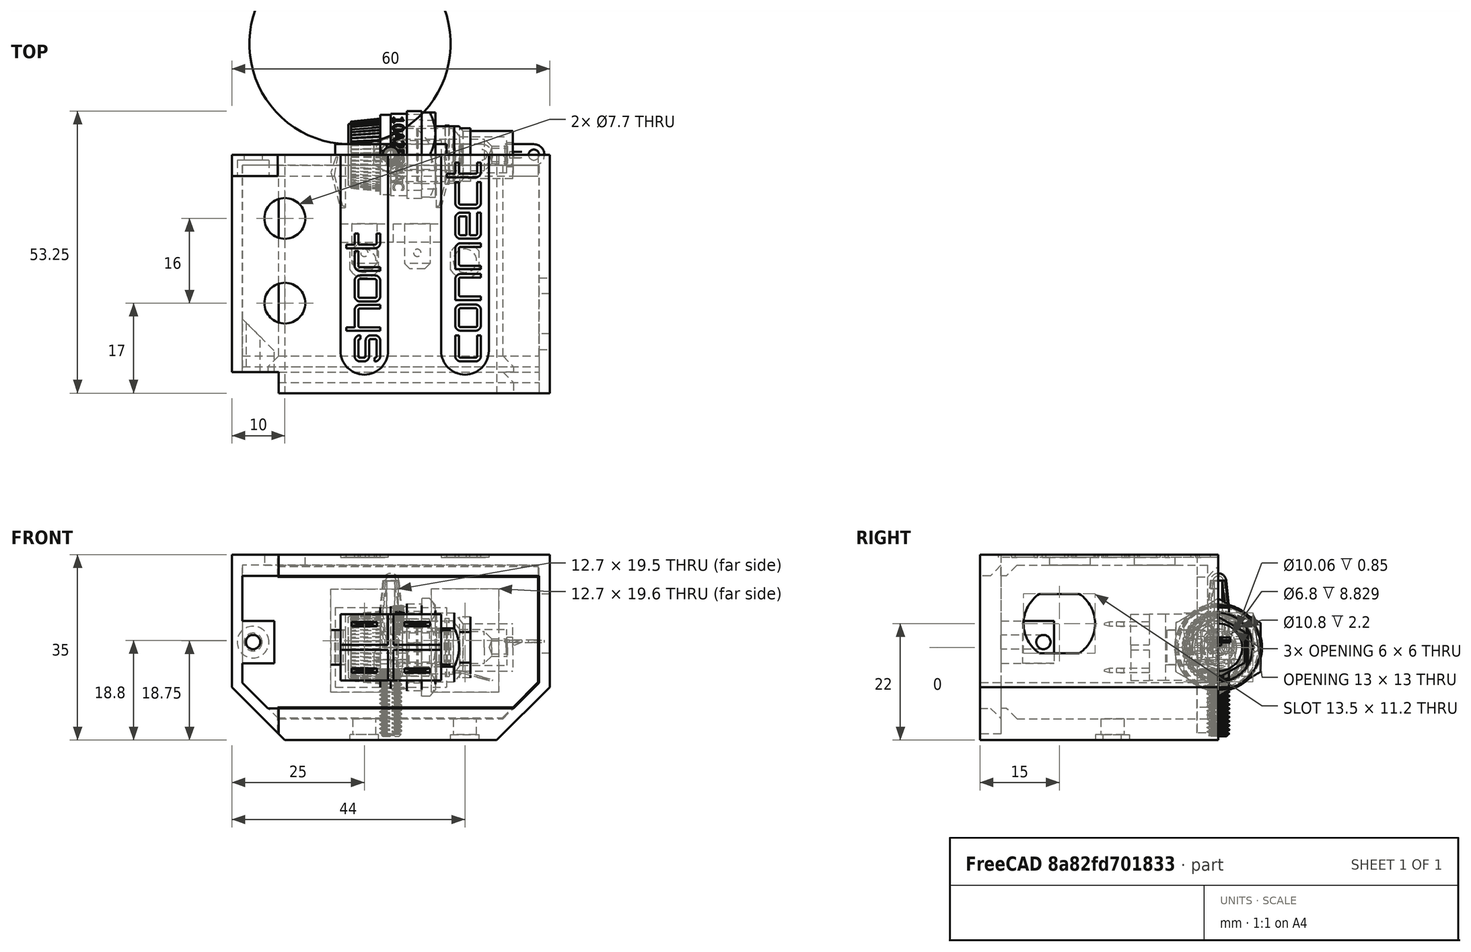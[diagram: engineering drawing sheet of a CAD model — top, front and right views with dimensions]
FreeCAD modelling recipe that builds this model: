
FCSTD DOCUMENT  (FreeCAD 1.0R38641 +468 (Git))
Label: multimeter_module
License: All rights reserved
LicenseURL: http://en.wikipedia.org/wiki/All_rights_reserved
objects: Sketcher::SketchObject×18, PartDesign::Pocket×12, Part::FeaturePython×11, App::Link×9, App::FeaturePython×9, Part::Part2DObjectPython×8, PartDesign::Body×6, PartDesign::Pad×5, Part::Feature×4, PartDesign::FeatureBase×4, PartDesign::Plane×3, PartDesign::Mirrored×3, App::DocumentObjectGroup×2, Part::Extrusion×2, Spreadsheet::Sheet×1, Image::ImagePlane×1, PartDesign::ShapeBinder×1, PartDesign::Line×1, PartDesign::Groove×1, Part::MultiFuse×1, +2 more types
note: 141 computed .brp shape members not serialized (recipe doc carries the construction recipe); baked Part::Feature solids carry a one-line shape summary decoded from their .brp

FEATURE [Spreadsheet::Sheet] Spreadsheet
  cells = B1='Print; C1='Nominal; A2='Length; B2(Length)=60; A3='Width; B3(Width)=45; A4='Height; B4(Height)=35; A5='Thickness; B5(Thickness)=2; A6='ThicknessBottom; B6(ThicknessBottom)=4; A7='SwitchWidth; B7(SwitchWidth)=12.7; C7=12.5; A8='SwitchHeight; B8(SwitchHeight)=19.6; C8=19; A9='SwitchDistance; B9(SwitchDistance)=19; A10='PlugDiameter; B10(PlugDiameter)=4.4; C10=4; A11='PlugPocketLength; B11(PlugPocketLength)=6.4; C11=6; A12='PlugPocketWidth; B12(PlugPocketWidth)=5.4; C12=5; A13='PlugDistance; B13(PlugDistance)=19; A14='PlugOffset; B14(PlugOffset)=16; A15='SocketDiameter; B15(SocketDiameter)=7.7; C15=7.3; A16='SocketDistance; B16(SocketDistance)=16; A17='FuseWidth; B17(FuseWidth)=11.2; C17=11.2; A18='FuseHeight; B18(FuseHeight)=13.5; C18=13.5; A19='PullChamferDepth; B19(PullChamferDepth)=10; A20='ThreadedHoleDiameter; B20(ThreadedHoleDiameter)=2.7; C20=3; A21='ScrewHoleRadius; B21(ScrewHoleRadius)=1.7; C21=1.5; A22='ScrewHeadRadius; B22(ScrewHeadRadius)=3
FEATURE [Sketcher::SketchObject] Sketch
  ArcFitTolerance = 1e-06
  AttachmentSupport = -> [XZ_Plane]
  FullyConstrained = true
  MakeInternals = false
  MapMode = 5
  Placement = pos=(0,0,0) rot=(1,0,0;1.5708rad)
  expr: Constraints[10] = Spreadsheet.Height
  expr: Constraints[9] = Spreadsheet.Length
  sketch-geometry (5):
    g0: LineSegment StartX=-30 StartY=-17.5 StartZ=0 EndX=30 EndY=-17.5 EndZ=0
    g1: LineSegment StartX=30 StartY=-17.5 StartZ=0 EndX=30 EndY=17.5 EndZ=0
    g2: LineSegment StartX=30 StartY=17.5 StartZ=0 EndX=-30 EndY=17.5 EndZ=0
    g3: LineSegment StartX=-30 StartY=17.5 StartZ=0 EndX=-30 EndY=-17.5 EndZ=0
    g4: GeomPoint [constr] X=0 Y=0 Z=0
  constraints (12):
    c: Coincident(g0,g1)
    c: Coincident(g1,g2)
    c: Coincident(g2,g3)
    c: Coincident(g3,g0)
    c: Horizontal(g0)
    c: Horizontal(g2)
    c: Vertical(g1)
    c: Vertical(g3)
    c: Symmetric(g2,g0,g4)
    c: Distance(g1,g3) = 60
    c: Distance(g0,g2) = 35
    c: Coincident(g4,g-1)
FEATURE [PartDesign::Pad] Pad
  Direction = (0,-1,2e-16)
  Length = 45
  Length2 = 10
  Placement = pos=(0,0,0) rot=(1,0,0;1.5708rad)
  Profile = -> Sketch
  ReferenceAxis = -> Sketch [N_Axis]
  Refine = true
  Suppressed = false
  Type = 0
  expr: Length = Spreadsheet.Width
FEATURE [Sketcher::SketchObject] Sketch001
  ArcFitTolerance = 1e-06
  AttachmentSupport = -> [Pad]
  ExternalGeometry = -> [Pad]
  FullyConstrained = true
  MakeInternals = false
  MapMode = 5
  Placement = pos=(0,-45,0) rot=(1,0,0;1.5708rad)
  expr: Constraints[10] = Spreadsheet.Length - 2 * Spreadsheet.Thickness
  expr: Constraints[11] = Spreadsheet.Thickness
  expr: Constraints[12] = Spreadsheet.Thickness
  expr: Constraints[9] = Spreadsheet.Height - Spreadsheet.Thickness - Spreadsheet.ThicknessBottom
  sketch-geometry (5):
    g0: LineSegment StartX=28 StartY=-13.5 StartZ=0 EndX=28 EndY=15.5 EndZ=0
    g1: LineSegment StartX=28 StartY=15.5 StartZ=0 EndX=-28 EndY=15.5 EndZ=0
    g2: LineSegment StartX=-28 StartY=15.5 StartZ=0 EndX=-28 EndY=-13.5 EndZ=0
    g3: LineSegment StartX=-28 StartY=-13.5 StartZ=0 EndX=28 EndY=-13.5 EndZ=0
    g4: GeomPoint [constr] X=0 Y=0 Z=0
  constraints (13):
    c: Coincident(g0,g1)
    c: Coincident(g1,g2)
    c: Coincident(g2,g3)
    c: Coincident(g3,g0)
    c: Vertical(g0)
    c: Vertical(g2)
    c: Horizontal(g1)
    c: Horizontal(g3)
    c: Coincident(g4,g-1)
    c: DistanceY(g0,g0) = 29
    c: DistanceX(g3,g3) = 56
    c: Distance(g-4,g1) = 2
    c: Distance(g-3,g2) = 2
FEATURE [PartDesign::Pocket] Pocket  label="Box inside"
  BaseFeature = -> Pad
  Direction = (0,1,-2e-16)
  Length = 43
  Length2 = 5
  Placement = pos=(0,0,0) rot=(1,0,0;1.5708rad)
  Profile = -> Sketch001
  ReferenceAxis = -> Sketch001 [N_Axis]
  Refine = true
  Suppressed = false
  Type = 0
  expr: Length = Spreadsheet.Width - Spreadsheet.Thickness
FEATURE [Sketcher::SketchObject] Sketch003
  ArcFitTolerance = 1e-06
  AttachmentSupport = -> [Pocket]
  ExternalGeometry = -> [Pocket]
  FullyConstrained = true
  MakeInternals = false
  MapMode = 5
  Placement = pos=(0,0,0) rot=(-1,0,0;1.5708rad)
  expr: Constraints[19] = Spreadsheet.SwitchWidth
  expr: Constraints[21] = Spreadsheet.SwitchDistance
  expr: Constraints[26] = Spreadsheet.PlugOffset
  expr: Constraints[8] = Spreadsheet.SwitchWidth
  expr: Constraints[9] = Spreadsheet.SwitchHeight
  sketch-geometry (11):
    g0: LineSegment StartX=7.65 StartY=-11.1 StartZ=0 EndX=20.35 EndY=-11.1 EndZ=0
    g1: LineSegment StartX=20.35 StartY=-11.1 StartZ=0 EndX=20.35 EndY=8.5 EndZ=0
    g2: LineSegment StartX=20.35 StartY=8.5 StartZ=0 EndX=7.65 EndY=8.5 EndZ=0
    g3: LineSegment StartX=7.65 StartY=8.5 StartZ=0 EndX=7.65 EndY=-11.1 EndZ=0
    g4: GeomPoint [constr] X=14 Y=-1.3 Z=0
    g5: LineSegment StartX=-11.35 StartY=-11 StartZ=0 EndX=1.35 EndY=-11 EndZ=0
    g6: LineSegment StartX=1.35 StartY=-11 StartZ=0 EndX=1.35 EndY=8.5 EndZ=0
    g7: LineSegment StartX=1.35 StartY=8.5 StartZ=0 EndX=-11.35 EndY=8.5 EndZ=0
    g8: LineSegment StartX=-11.35 StartY=8.5 StartZ=0 EndX=-11.35 EndY=-11 EndZ=0
    g9: GeomPoint [constr] X=-5 Y=-1.25 Z=0
    g10: LineSegment [constr] StartX=-11.35 StartY=8.5 StartZ=0 EndX=20.35 EndY=8.5 EndZ=0
  constraints (28):
    c: Coincident(g0,g1)
    c: Coincident(g1,g2)
    c: Coincident(g2,g3)
    c: Coincident(g3,g0)
    c: Horizontal(g0)
    c: Horizontal(g2)
    c: Vertical(g1)
    c: Vertical(g3)
    c: Distance(g1,g3) = 12.7
    c: Distance(g0,g2) = 19.6
    c: Coincident(g5,g6)
    c: Coincident(g6,g7)
    c: Coincident(g7,g8)
    c: Coincident(g8,g5)
    c: Horizontal(g5)
    c: Horizontal(g7)
    c: Vertical(g6)
    c: Vertical(g8)
    c: Symmetric(g7,g5,g9) = 13
    c: Distance(g6,g8) = 12.7
    c: Distance(g5,g7) = 19.5
    c: DistanceX(g9,g4) = 19
    c: Distance(g-3,g7) = 9
    c: Coincident(g10,g7)
    c: Coincident(g10,g1)
    c: Horizontal(g10)
    c: Distance(g4,g-4) = 16
    c: Symmetric(g0,g1,g4)
FEATURE [PartDesign::Pocket] Pocket001  label="Switch holes"
  BaseFeature = -> Pocket
  Direction = (0,-1,-2e-16)
  Length = 3
  Length2 = 5
  Placement = pos=(0,0,0) rot=(1,0,0;1.5708rad)
  Profile = -> Sketch003
  ReferenceAxis = -> Sketch003 [N_Axis]
  Refine = true
  Suppressed = false
  Type = 0
  expr: Length = Spreadsheet.Thickness + 1
FEATURE [Sketcher::SketchObject] Sketch004
  ArcFitTolerance = 1e-06
  AttachmentSupport = -> [Pocket001]
  ExternalGeometry = -> [Pocket001]
  FullyConstrained = true
  MakeInternals = false
  MapMode = 5
  Placement = pos=(0,-7.7e-15,-17.5) rot=(1,0,0;3.14159rad)
  expr: Constraints[0] = Spreadsheet.PlugDiameter
  expr: Constraints[1] = Spreadsheet.PlugDiameter
  expr: Constraints[5] = Spreadsheet.PlugOffset
  expr: Constraints[7] = Spreadsheet.PlugDistance
  sketch-geometry (3):
    g0: Circle CenterX=14 CenterY=20 CenterZ=0 NormalX=0 NormalY=0 NormalZ=1 AngleXU=0 Radius=2.2
    g1: Circle CenterX=-5 CenterY=20 CenterZ=0 NormalX=0 NormalY=0 NormalZ=1 AngleXU=0 Radius=2.2
    g2: LineSegment [constr] StartX=-5 StartY=20 StartZ=0 EndX=14 EndY=20 EndZ=0
  constraints (8):
    c: Diameter(g0) = 4.4
    c: Diameter(g1) = 4.4
    c: Coincident(g2,g1)
    c: Coincident(g2,g0)
    c: Horizontal(g2)
    c: Distance(g0,g-4) = 16
    c: DistanceY(g-1,g0) = 20
    c: DistanceX(g1,g0) = 19
FEATURE [PartDesign::Pocket] Pocket002  label="Plug holes"
  BaseFeature = -> Pocket001
  Direction = (0,0,1)
  Length = 5
  Length2 = 5
  Placement = pos=(0,0,0) rot=(1,0,0;1.5708rad)
  Profile = -> Sketch004
  ReferenceAxis = -> Sketch004 [N_Axis]
  Refine = true
  Suppressed = false
  Type = 0
  expr: Length = Spreadsheet.ThicknessBottom + 1
FEATURE [Sketcher::SketchObject] Sketch005
  ArcFitTolerance = 1e-06
  AttachmentSupport = -> [Pocket002]
  ExternalGeometry = -> [Pocket002]
  FullyConstrained = true
  MakeInternals = false
  MapMode = 5
  Placement = pos=(0,7.7e-15,17.5) rot=(0,0,1;3.14159rad)
  expr: Constraints[0] = Spreadsheet.SocketDiameter
  expr: Constraints[1] = Spreadsheet.SocketDiameter
  expr: Constraints[5] = Spreadsheet.SocketDistance
  sketch-geometry (3):
    g0: Circle CenterX=20 CenterY=28 CenterZ=0 NormalX=0 NormalY=0 NormalZ=1 AngleXU=0 Radius=3.85
    g1: Circle CenterX=20 CenterY=12 CenterZ=0 NormalX=0 NormalY=0 NormalZ=1 AngleXU=0 Radius=3.85
    g2: LineSegment [constr] StartX=20 StartY=28 StartZ=0 EndX=20 EndY=12 EndZ=0
  constraints (8):
    c: Diameter(g0) = 7.7
    c: Diameter(g1) = 7.7
    c: Coincident(g2,g0)
    c: Coincident(g2,g1)
    c: Vertical(g2)
    c: DistanceY(g1,g0) = 16
    c: Distance(g1,g-1) = 12
    c: Distance(g0,g-3) = 50
FEATURE [PartDesign::Pocket] Pocket003  label="Socket holes"
  BaseFeature = -> Pocket002
  Direction = (0,0,-1)
  Length = 3
  Length2 = 5
  Placement = pos=(0,0,0) rot=(1,0,0;1.5708rad)
  Profile = -> Sketch005
  ReferenceAxis = -> Sketch005 [N_Axis]
  Refine = true
  Suppressed = false
  Type = 0
  expr: Length = Spreadsheet.Thickness + 1
FEATURE [Sketcher::SketchObject] Sketch006
  ArcFitTolerance = 1e-06
  AttachmentSupport = -> [Pocket003]
  ExternalGeometry = -> [Pocket003]
  FullyConstrained = true
  MakeInternals = false
  MapMode = 5
  Placement = pos=(30,0,0) rot=(0.707107,0,0.707107;3.14159rad)
  expr: Constraints[11] = Spreadsheet.FuseHeight / 2
  expr: Constraints[12] = Spreadsheet.FuseHeight / 2
  expr: Constraints[1] = Spreadsheet.FuseWidth
  sketch-geometry (4):
    g0: LineSegment StartX=-1.1 StartY=33.7686 StartZ=0 EndX=-1.1 EndY=26.2314 EndZ=0
    g1: LineSegment StartX=10.1 StartY=33.7686 StartZ=0 EndX=10.1 EndY=26.2314 EndZ=0
    g2: ArcOfCircle CenterX=4.5 CenterY=30 CenterZ=0 NormalX=0 NormalY=0 NormalZ=1 AngleXU=0 Radius=6.75 StartAngle=0.592352 EndAngle=2.54924
    g3: ArcOfCircle CenterX=4.5 CenterY=30 CenterZ=0 NormalX=0 NormalY=0 NormalZ=1 AngleXU=0 Radius=6.75 StartAngle=3.73394 EndAngle=5.69083
  constraints (13):
    c: Coincident(g3,g2)
    c: Distance(g0,g1) = 11.2
    c: Distance(g2,g-3) = 22
    c: Vertical(g0)
    c: Vertical(g1)
    c: Distance(g2,g-4) = 30
    c: Equal(g0,g1)
    c: Coincident(g1,g2)
    c: Coincident(g1,g3)
    c: Coincident(g0,g3)
    c: Coincident(g0,g2)
    c: Radius(g3) = 6.75
    c: Radius(g2) = 6.75
FEATURE [PartDesign::Pocket] Pocket004  label="Fuse hole"
  BaseFeature = -> Pocket003
  Direction = (-1,0,2e-16)
  Length = 5
  Length2 = 5
  Placement = pos=(0,0,0) rot=(1,0,0;1.5708rad)
  Profile = -> Sketch006
  ReferenceAxis = -> Sketch006 [N_Axis]
  Refine = true
  Suppressed = false
  Type = 0
  expr: Length = Spreadsheet.ThicknessBottom + 1
FEATURE [Part::Feature] Part__Feature008  label="BK2-HTC-603M"
  shape: bbox 62.61 x 18.49 x 88.41 mm, 497 faces (baked)
FEATURE [Part::Feature] Part__Feature009  label="94E3D872-CF5D-4008-881E-EF016884AD34"
  shape: bbox 6.35 x 7.333 x 30.94 mm, 102 faces (baked)
FEATURE [Part::Feature] Part__Feature010  label="F9A9451F-7465-43D9-86F5-C9F07849855A"
  shape: bbox 22 x 11 x 11.55 mm, 46 faces (baked)
FEATURE [Part::Feature] Part__Feature011  label="a8l-11-15n1"
  shape: bbox 22.6 x 27.1 x 15 mm, 93 faces (baked)
FEATURE [PartDesign::FeatureBase] BaseFeature
  BaseFeature = -> Part__Feature011
  Suppressed = false
FEATURE [PartDesign::Body] Body001  label="Switch a8l-11-15n11"
  AllowCompound = false
  BaseFeature = -> Part__Feature011
  Group = -> [BaseFeature]
  Origin = -> Origin002
  Tip = -> BaseFeature
FEATURE [PartDesign::FeatureBase] BaseFeature001
  BaseFeature = -> Part__Feature010
  Suppressed = false
FEATURE [PartDesign::Body] Body004  label="Socket 4mm"
  AllowCompound = false
  BaseFeature = -> Part__Feature010
  Group = -> [BaseFeature001]
  Origin = -> Origin005
  Tip = -> BaseFeature001
FEATURE [PartDesign::FeatureBase] BaseFeature002
  BaseFeature = -> Part__Feature009
  Suppressed = false
FEATURE [PartDesign::Body] Body003  label="Plug 4mm"
  AllowCompound = false
  BaseFeature = -> Part__Feature009
  Group = -> [BaseFeature002]
  Origin = -> Origin004
  Tip = -> BaseFeature002
FEATURE [PartDesign::FeatureBase] BaseFeature003
  BaseFeature = -> Part__Feature008
  Suppressed = false
FEATURE [PartDesign::Body] Body002  label="Fuse holder BK8-HTC-603M001"
  AllowCompound = false
  BaseFeature = -> Part__Feature008
  Group = -> [BaseFeature003]
  Origin = -> Origin003
  Tip = -> BaseFeature003
FEATURE [App::DocumentObjectGroup] Group  label="3D models of components"
  Group = -> [Part__Feature008,Part__Feature009,Part__Feature010,Part__Feature011]
FEATURE [App::Link] Switch_a8l_11_15n11  label="Switch CONNECT"
  LinkPlacement = pos=(14.1,2e-16,1.3) rot=(0,-1,0;1.5708rad)
  LinkedObject = -> Body001
  Placement = pos=(14.1,2e-16,1.3) rot=(0,-1,0;1.5708rad)
FEATURE [App::Link] Switch_a8l_11_15n012  label="Switch SHORT"
  LinkPlacement = pos=(-4.9,-2.8e-15,1.2) rot=(0,-1,0;1.5708rad)
  LinkedObject = -> Body001
  Placement = pos=(-4.9,-2.8e-15,1.2) rot=(0,-1,0;1.5708rad)
FEATURE [App::Link] Socket_4mm  label="Socket +"
  LinkPlacement = pos=(-20,-28,22.3572) rot=(-0.57735,0.57735,0.57735;2.0944rad)
  LinkedObject = -> Body004
  Placement = pos=(-20,-28,22.3572) rot=(-0.57735,0.57735,0.57735;2.0944rad)
FEATURE [App::Link] Socket_4mm001  label="Socket -"
  LinkPlacement = pos=(-20,-12,22.3572) rot=(-0.57735,0.57735,0.57735;2.0944rad)
  LinkedObject = -> Body004
  Placement = pos=(-20,-12,22.3572) rot=(-0.57735,0.57735,0.57735;2.0944rad)
FEATURE [Sketcher::SketchObject] Sketch007
  ArcFitTolerance = 1e-06
  AttachmentSupport = -> [Pocket004]
  ExternalGeometry = -> [Pocket004]
  FullyConstrained = true
  MakeInternals = false
  MapMode = 5
  Placement = pos=(0,-7.7e-15,-17.5) rot=(1,0,0;3.14159rad)
  expr: Constraints[13] = Spreadsheet.PlugPocketLength
  expr: Constraints[22] = Spreadsheet.PlugPocketWidth
  expr: Constraints[23] = Spreadsheet.PlugPocketWidth
  expr: Constraints[3] = Spreadsheet.PlugPocketLength
  sketch-geometry (8):
    g0: LineSegment StartX=11.3 StartY=21.7176 StartZ=0 EndX=11.3 EndY=18.2824 EndZ=0
    g1: LineSegment StartX=16.7 StartY=21.7176 StartZ=0 EndX=16.7 EndY=18.2824 EndZ=0
    g2: ArcOfCircle CenterX=14 CenterY=20 CenterZ=0 NormalX=0 NormalY=0 NormalZ=1 AngleXU=0 Radius=3.2 StartAngle=3.70816 EndAngle=5.71662
    g3: ArcOfCircle CenterX=14 CenterY=20 CenterZ=0 NormalX=0 NormalY=0 NormalZ=1 AngleXU=0 Radius=3.2 StartAngle=0.566564 EndAngle=2.57503
    g4: LineSegment StartX=-7.7 StartY=21.7176 StartZ=0 EndX=-7.7 EndY=18.2824 EndZ=0
    g5: LineSegment StartX=-2.3 StartY=21.7176 StartZ=0 EndX=-2.3 EndY=18.2824 EndZ=0
    g6: ArcOfCircle CenterX=-5 CenterY=20 CenterZ=0 NormalX=0 NormalY=0 NormalZ=1 AngleXU=0 Radius=3.2 StartAngle=3.70816 EndAngle=5.71662
    g7: ArcOfCircle CenterX=-5 CenterY=20 CenterZ=0 NormalX=0 NormalY=0 NormalZ=1 AngleXU=0 Radius=3.2 StartAngle=0.566564 EndAngle=2.57503
  constraints (26):
    c: Vertical(g0)
    c: Vertical(g1)
    c: Coincident(g2,g-4)
    c: Diameter(g2) = 6.4
    c: PointOnObject(g1,g3)
    c: Coincident(g3,g0)
    c: Coincident(g2,g0)
    c: Equal(g2,g3)
    c: Coincident(g2,g1)
    c: PointOnObject(g3,g1)
    c: Coincident(g2,g3)
    c: Vertical(g5)
    c: Vertical(g4)
    c: Diameter(g6) = 6.4
    c: Coincident(g6,g-3)
    c: PointOnObject(g5,g7)
    c: Coincident(g7,g4)
    c: Coincident(g6,g4)
    c: Equal(g6,g7)
    c: Coincident(g6,g5)
    c: PointOnObject(g7,g5)
    c: Coincident(g6,g7)
    c: Distance(g1,g0) = 5.4
    c: Distance(g5,g4) = 5.4
    c: Equal(g4,g5)
    c: Equal(g0,g1)
FEATURE [PartDesign::Pocket] Pocket005  label="Plug pockets"
  AttacherType = Attacher::AttachEngine3D
  BaseFeature = -> Pocket004
  Direction = (0,0,1)
  Length = 1
  Length2 = 5
  Placement = pos=(0,0,0) rot=(1,0,0;1.5708rad)
  Profile = -> Sketch007
  ReferenceAxis = -> Sketch007 [N_Axis]
  Refine = true
  Suppressed = false
  Type = 0
FEATURE [App::Link] Plug_4mm  label="Plug COM"
  LinkPlacement = pos=(-5,-20,-20.564) rot=(1,0,0;3.14159rad)
  LinkedObject = -> Body003
  Placement = pos=(-5,-20,-20.564) rot=(1,0,0;3.14159rad)
FEATURE [App::Link] Plug_4mm001  label="Plug mA"
  LinkPlacement = pos=(14,-20,-20.564) rot=(1,0,0;3.14159rad)
  LinkedObject = -> Body003
  Placement = pos=(14,-20,-20.564) rot=(1,0,0;3.14159rad)
FEATURE [Image::ImagePlane] fluke_87v  label="fluke-87v"
  AttacherType = Attacher::AttachEngine3D
  MapMode = 5
  Placement = pos=(5.5,-76,-22) rot=(0,0,1;3.14159rad)
  XSize = 108.111
  YSize = 207.109
FEATURE [Sketcher::SketchObject] Sketch008
  ArcFitTolerance = 1e-06
  AttachmentSupport = -> [Pocket005]
  ExternalGeometry = -> [Pocket005]
  FullyConstrained = true
  MakeInternals = false
  MapMode = 5
  Placement = pos=(0,0,0) rot=(-1,0,0;1.5708rad)
  expr: Constraints[6] = Spreadsheet.PullChamferDepth
  expr: Constraints[7] = Spreadsheet.PullChamferDepth
  sketch-geometry (3):
    g0: LineSegment StartX=30 StartY=17.5 StartZ=0 EndX=30 EndY=7.5 EndZ=0
    g1: LineSegment StartX=30 StartY=17.5 StartZ=0 EndX=20 EndY=17.5 EndZ=0
    g2: LineSegment StartX=20 StartY=17.5 StartZ=0 EndX=30 EndY=7.5 EndZ=0
  constraints (8):
    c: Coincident(g0,g-4)
    c: PointOnObject(g0,g-4)
    c: Coincident(g1,g0)
    c: Horizontal(g1)
    c: Coincident(g2,g1)
    c: Coincident(g2,g0)
    c: DistanceY(g0,g0) = 10
    c: DistanceX(g1,g0) = 10
FEATURE [PartDesign::Plane] DatumPlane  label="Lid shelves symmetry plane"
  AttachmentOffset = pos=(0,0,14.5) rot=(0,0,1;0rad)
  Length = 72.9615
  MapMode = 5
  Placement = pos=(0,6.8e-15,1) rot=(1,0,0;3.14159rad)
  ResizeMode = 0
  Width = 82.9615
  expr: .AttachmentOffset.Base.z = (Spreadsheet.Height - Spreadsheet.Thickness - Spreadsheet.ThicknessBottom) / 2
FEATURE [Sketcher::SketchObject] Sketch013
  ArcFitTolerance = 1e-06
  FullyConstrained = true
  MakeInternals = false
  MapMode = 5
  Placement = pos=(0,7.7e-15,17.5) rot=(0,0,1;3.14159rad)
  sketch-geometry (4):
    g0: LineSegment StartX=30 StartY=45 StartZ=0 EndX=21.1716 EndY=45 EndZ=0
    g1: LineSegment StartX=21.1716 StartY=45 StartZ=0 EndX=21.1716 EndY=41 EndZ=0
    g2: LineSegment StartX=21.1716 StartY=41 StartZ=0 EndX=30 EndY=41 EndZ=0
    g3: LineSegment StartX=30 StartY=41 StartZ=0 EndX=30 EndY=45 EndZ=0
  constraints (10):
    c: Coincident(g0,g1)
    c: Coincident(g1,g2)
    c: Coincident(g2,g3)
    c: Coincident(g3,g0)
    c: Horizontal(g0)
    c: Horizontal(g2)
    c: Vertical(g1)
    c: Vertical(g3)
    c: Coincident(g0,g-4)
    c: Coincident(g1,g-5)
FEATURE [Sketcher::SketchObject] Sketch014
  ArcFitTolerance = 1e-06
  AttachmentSupport = -> [DatumPlane]
  FullyConstrained = true
  MakeInternals = false
  MapMode = 5
  Placement = pos=(0,6.8e-15,1) rot=(1,0,0;3.14159rad)
  sketch-geometry (4):
    g0: LineSegment StartX=-28 StartY=41 StartZ=0 EndX=-22 EndY=41 EndZ=0
    g1: LineSegment StartX=-22 StartY=41 StartZ=0 EndX=-22 EndY=37 EndZ=0
    g2: LineSegment StartX=-28 StartY=41 StartZ=0 EndX=-28 EndY=31 EndZ=0
    g3: LineSegment StartX=-28 StartY=31 StartZ=0 EndX=-22 EndY=37 EndZ=0
  constraints (11):
    c: Coincident(g0,g-4)
    c: PointOnObject(g0,g-4)
    c: Coincident(g1,g0)
    c: Parallel(g2,g-3)
    c: Coincident(g2,g0)
    c: Coincident(g3,g2)
    c: Coincident(g3,g1)
    c: DistanceX(g0,g0) = 6
    c: Vertical(g1)
    c: Angle(g3,g2) = 0.785398
    c: DistanceY(g1,g0) = 4
FEATURE [App::Link] Lid  label="Lid001"
  LinkPlacement = pos=(-1.72159e-05,-41,-0.000447514) rot=(0,1,0;1.7e-05rad)
  LinkedObject = -> Body005
  Placement = pos=(-1.72159e-05,-41,-0.000447514) rot=(0,1,0;1.7e-05rad)
FEATURE [App::FeaturePython] Joint001  label="Fixed_connect"  # Assembly joint (typed FeaturePython)
  Activated = true
  AngleMax = 0
  AngleMin = 0
  Detach1 = false
  Detach2 = false
  Distance = 0
  Distance2 = 0
  EnableAngleMax = false
  EnableAngleMin = false
  EnableLengthMax = false
  EnableLengthMin = false
  JointType = 0 (Fixed)
  LengthMax = 0
  LengthMin = 0
  Offset2 = pos=(0,0,0) rot=(0,0,1;3.14159rad)
  Placement1 = pos=(-7e-16,-1e-15,-6.25) rot=(-0.707107,0,0.707107;3.14159rad)
  Placement2 = pos=(20.35,0,1.3) rot=(1,0,0;3.14159rad)
  Reference1 = -> Assembly [Switch_a8l_11_15n11.Edge173,Switch_a8l_11_15n11.Edge173]
  Reference2 = -> Assembly [Box.Edge54,Box.Edge54]
FEATURE [App::FeaturePython] Joint002  label="Fixed_short"  # Assembly joint (typed FeaturePython)
  Activated = true
  AngleMax = 0
  AngleMin = 0
  Detach1 = false
  Detach2 = false
  Distance = 0
  Distance2 = 0
  EnableAngleMax = false
  EnableAngleMin = false
  EnableLengthMax = false
  EnableLengthMin = false
  JointType = 0 (Fixed)
  LengthMax = 0
  LengthMin = 0
  Offset2 = pos=(0,0,1.2) rot=(0,0,1;3.14159rad)
  Placement1 = pos=(8.6,0,-6.25) rot=(-0.707107,0,0.707107;3.14159rad)
  Placement2 = pos=(1.35,-2e-15,9.8) rot=(1,0,0;3.14159rad)
  Reference1 = -> Assembly [Switch_a8l_11_15n012.Edge173,Switch_a8l_11_15n012.Vertex121]
  Reference2 = -> Assembly [Box.Edge50,Box.Vertex42]
FEATURE [App::FeaturePython] Joint014  label="Fixed_plus"  # Assembly joint (typed FeaturePython)
  Activated = true
  AngleMax = 0
  AngleMin = 0
  Detach1 = false
  Detach2 = false
  Distance = 0
  Distance2 = 0
  EnableAngleMax = false
  EnableAngleMin = false
  EnableLengthMax = false
  EnableLengthMin = false
  JointType = 0 (Fixed)
  LengthMax = 0
  LengthMin = 0
  Placement1 = pos=(4.85718,0,0) rot=(0.57735,0.57735,0.57735;2.0944rad)
  Placement2 = pos=(-20,-28,17.5) rot=(0,0,1;3.14159rad)
  Reference1 = -> Assembly [Socket_4mm.Edge38,Socket_4mm.Edge38]
  Reference2 = -> Assembly [Box.Edge104,Box.Edge104]
FEATURE [App::FeaturePython] Joint015  label="Fixed_minus"  # Assembly joint (typed FeaturePython)
  Activated = true
  AngleMax = 0
  AngleMin = 0
  Detach1 = false
  Detach2 = false
  Distance = 0
  Distance2 = 0
  EnableAngleMax = false
  EnableAngleMin = false
  EnableLengthMax = false
  EnableLengthMin = false
  JointType = 0 (Fixed)
  LengthMax = 0
  LengthMin = 0
  Placement1 = pos=(4.85718,0,1.8e-15) rot=(0.57735,0.57735,0.57735;2.0944rad)
  Placement2 = pos=(-20,-12,17.5) rot=(0,0,1;3.14159rad)
  Reference1 = -> Assembly [Socket_4mm001.Edge38,Socket_4mm001.Edge38]
  Reference2 = -> Assembly [Box.Edge105,Box.Edge105]
FEATURE [App::Link] Fuse_holder_BK8_HTC_603M001  label="Fuse holder"
  LinkPlacement = pos=(32.7915,-30,4.7) rot=(0,0.707107,0.707107;3.14159rad)
  LinkedObject = -> Body002
  Placement = pos=(32.7915,-30,4.7) rot=(0,0.707107,0.707107;3.14159rad)
FEATURE [App::Link] Box  label="Box001"
  LinkedObject = -> Body
FEATURE [App::FeaturePython] GroundedJoint  # Assembly grounded joint (typed FeaturePython)
  ObjectToGround = -> Box
FEATURE [App::FeaturePython] Joint  label="Fixed_fuse"  # Assembly joint (typed FeaturePython)
  Activated = true
  AngleMax = 0
  AngleMin = 0
  Detach1 = false
  Detach2 = false
  Distance = 0
  Distance2 = 0
  EnableAngleMax = false
  EnableAngleMin = false
  EnableLengthMax = false
  EnableLengthMin = false
  JointType = 0 (Fixed)
  LengthMax = 0
  LengthMin = 0
  Offset1 = pos=(0,-4,0) rot=(0,0,1;0rad)
  Offset2 = pos=(0,0,0) rot=(0,0,1;3.14159rad)
  Placement1 = pos=(3.79152,5.4,-3.6e-15) rot=(0.57735,0.57735,-0.57735;2.0944rad)
  Placement2 = pos=(29,-30,10.1) rot=(0.707107,-0.707107,0;3.14159rad)
  Reference1 = -> Assembly [Fuse_holder_BK8_HTC_603M001.Face48,Fuse_holder_BK8_HTC_603M001.Face48]
  Reference2 = -> Assembly [Box.Face51,Box.Face51]
FEATURE [App::FeaturePython] Joint016  label="Fixed_com"  # Assembly joint (typed FeaturePython)
  Activated = true
  AngleMax = 0
  AngleMin = 0
  Detach1 = false
  Detach2 = false
  Distance = 0
  Distance2 = 0
  EnableAngleMax = false
  EnableAngleMin = false
  EnableLengthMax = false
  EnableLengthMin = false
  JointType = 0 (Fixed)
  LengthMax = 0
  LengthMin = 0
  Placement1 = pos=(0,0,-4.064) rot=(0,0,1;0rad)
  Placement2 = pos=(-5,-20,-16.5) rot=(1,0,0;3.14159rad)
  Reference1 = -> Assembly [Plug_4mm.Edge166,Plug_4mm.Edge166]
  Reference2 = -> Assembly [Box.Edge21,Box.Edge21]
FEATURE [App::FeaturePython] Joint017  label="Fixed_mA"  # Assembly joint (typed FeaturePython)
  Activated = true
  AngleMax = 0
  AngleMin = 0
  Detach1 = false
  Detach2 = false
  Distance = 0
  Distance2 = 0
  EnableAngleMax = false
  EnableAngleMin = false
  EnableLengthMax = false
  EnableLengthMin = false
  JointType = 0 (Fixed)
  LengthMax = 0
  LengthMin = 0
  Placement1 = pos=(0,0,-4.064) rot=(0,0,1;0rad)
  Placement2 = pos=(14,-20,-16.5) rot=(1,0,0;3.14159rad)
  Reference1 = -> Assembly [Plug_4mm001.Edge166,Plug_4mm001.Edge166]
  Reference2 = -> Assembly [Box.Edge148,Box.Edge148]
FEATURE [Sketcher::SketchObject] Sketch021
  ArcFitTolerance = 1e-06
  AttachmentSupport = -> [Pocket005]
  ExternalGeometry = -> [Pocket005]
  FullyConstrained = true
  MakeInternals = false
  MapMode = 5
  Placement = pos=(-28,0,0) rot=(0.707107,0,0.707107;3.14159rad)
  sketch-geometry (7):
    g0: LineSegment StartX=-13.5 StartY=45 StartZ=0 EndX=-11.5 EndY=45 EndZ=0
    g1: LineSegment StartX=-11.5 StartY=45 StartZ=0 EndX=-11.5 EndY=43 EndZ=0
    g2: LineSegment StartX=-11.5 StartY=43 StartZ=0 EndX=-13.5 EndY=41 EndZ=0
    g3: LineSegment StartX=-13.5 StartY=41 StartZ=0 EndX=-11.5 EndY=41 EndZ=0
    g4: LineSegment StartX=-11.5 StartY=41 StartZ=0 EndX=-11.5 EndY=40 EndZ=0
    g5: LineSegment StartX=-11.5 StartY=40 StartZ=0 EndX=-13.5 EndY=38 EndZ=0
    g6: LineSegment StartX=-13.5 StartY=38 StartZ=0 EndX=-13.5 EndY=45 EndZ=0
  constraints (20):
    c: Coincident(g0,g-4)
    c: Coincident(g1,g0)
    c: Vertical(g1)
    c: Coincident(g2,g1)
    c: PointOnObject(g2,g-4)
    c: Coincident(g3,g2)
    c: Horizontal(g3)
    c: Coincident(g4,g3)
    c: Vertical(g4)
    c: Coincident(g5,g4)
    c: PointOnObject(g5,g-4)
    c: Coincident(g6,g5)
    c: Coincident(g6,g0)
    c: Horizontal(g0)
    c: Angle(g2,g6) = 0.785398
    c: Angle(g5,g6) = 0.785398
    c: DistanceX(g0,g0) = 2
    c: DistanceY(g1,g0) = 2
    c: Distance(g3,g4) = 1
    c: Equal(g0,g3)
FEATURE [PartDesign::Pad] Pad007  label="Lid shelf right"
  BaseFeature = -> Pocket005
  Direction = (1,0,-2e-16)
  Length = 10
  Length2 = 10
  Placement = pos=(0,0,0) rot=(1,0,0;1.5708rad)
  Profile = -> Sketch021
  ReferenceAxis = -> Sketch021 [N_Axis]
  Refine = true
  Suppressed = false
  Type = 1
FEATURE [PartDesign::Mirrored] Mirrored  label="Lid shelf left"
  BaseFeature = -> Pad007
  MirrorPlane = -> DatumPlane
  Originals = -> [Pad007]
  Placement = pos=(0,0,0) rot=(1,0,0;1.5708rad)
  Refine = true
  Suppressed = false
  TransformMode = 0
FEATURE [PartDesign::Pocket] Pocket006  label="Pull chamfer left"
  BaseFeature = -> Mirrored
  Direction = (0,-1,-2e-16)
  Length = 47
  Length2 = 5
  Placement = pos=(0,0,0) rot=(1,0,0;1.5708rad)
  Profile = -> Sketch008
  ReferenceAxis = -> Sketch008 [N_Axis]
  Refine = true
  Suppressed = false
  Type = 1
  expr: Length = Spreadsheet.Width + 2
FEATURE [Sketcher::SketchObject] Sketch009
  ArcFitTolerance = 1e-06
  AttachmentSupport = -> [Pocket006]
  ExternalGeometry = -> [Pocket006]
  FullyConstrained = true
  MakeInternals = false
  MapMode = 5
  Placement = pos=(0,0,0) rot=(-1,0,0;1.5708rad)
  expr: Constraints[9] = Spreadsheet.Thickness
  sketch-geometry (4):
    g0: LineSegment StartX=20 StartY=17.5 StartZ=0 EndX=30 EndY=7.5 EndZ=0
    g1: LineSegment StartX=20 StartY=17.5 StartZ=0 EndX=17.1716 EndY=17.5 EndZ=0
    g2: LineSegment StartX=30 StartY=7.5 StartZ=0 EndX=30 EndY=4.67157 EndZ=0
    g3: LineSegment StartX=17.1716 StartY=17.5 StartZ=0 EndX=30 EndY=4.67157 EndZ=0
  constraints (10):
    c: Coincident(g0,g-4)
    c: Coincident(g0,g-5)
    c: Coincident(g1,g0)
    c: PointOnObject(g1,g-3)
    c: Coincident(g2,g0)
    c: PointOnObject(g2,g-5)
    c: Coincident(g3,g1)
    c: Coincident(g3,g2)
    c: Parallel(g0,g3)
    c: Distance(g3,g0) = 2
FEATURE [PartDesign::Pad] Pad001  label="Pull chamfer left wall"
  BaseFeature = -> Pocket006
  Direction = (0,1,2e-16)
  Length = 45
  Length2 = 10
  Placement = pos=(0,0,0) rot=(1,0,0;1.5708rad)
  Profile = -> Sketch009
  ReferenceAxis = -> Sketch009 [N_Axis]
  Refine = true
  Reversed = true
  Suppressed = false
  Type = 1
  expr: Length = Spreadsheet.Width
FEATURE [PartDesign::Mirrored] Mirrored001  label="Pull chamfer right"
  BaseFeature = -> Pad001
  MirrorPlane = -> YZ_Plane
  Originals = -> [Pocket006]
  Placement = pos=(0,0,0) rot=(1,0,0;1.5708rad)
  Refine = true
  Suppressed = false
  TransformMode = 0
FEATURE [PartDesign::Mirrored] Mirrored002  label="Pull chamfer right wall"
  BaseFeature = -> Mirrored001
  MirrorPlane = -> YZ_Plane
  Originals = -> [Pad001]
  Placement = pos=(0,0,0) rot=(1,0,0;1.5708rad)
  Refine = true
  Suppressed = false
  TransformMode = 0
FEATURE [PartDesign::Pocket] Pocket008  label="Lid entrance"
  BaseFeature = -> Mirrored002
  Direction = (0,0,-1)
  Length = 5
  Length2 = 5
  Placement = pos=(0,0,0) rot=(1,0,0;1.5708rad)
  Profile = -> Sketch013
  ReferenceAxis = -> Sketch013 [N_Axis]
  Refine = true
  Suppressed = false
  Type = 1
FEATURE [PartDesign::Pad] Pad004  label="Screw holder"
  BaseFeature = -> Pocket008
  Direction = (0,0,-1)
  Length = 8
  Length2 = 10
  Midplane = true
  Placement = pos=(0,0,0) rot=(1,0,0;1.5708rad)
  Profile = -> Sketch014
  ReferenceAxis = -> Sketch014 [N_Axis]
  Refine = true
  Suppressed = false
  Type = 0
FEATURE [Sketcher::SketchObject] Sketch015
  ArcFitTolerance = 1e-06
  AttachmentSupport = -> [Pad004]
  ExternalGeometry = -> [Pad004]
  FullyConstrained = true
  MakeInternals = false
  MapMode = 5
  Placement = pos=(6.0955e-12,-41,1.341e-13) rot=(1,0,0;1.5708rad)
  expr: Constraints[9] = Spreadsheet.ThreadedHoleDiameter
  sketch-geometry (7):
    g0: LineSegment [constr] StartX=-22 StartY=5 StartZ=0 EndX=-30 EndY=5 EndZ=0
    g1: LineSegment [constr] StartX=-22 StartY=-3 StartZ=0 EndX=-30 EndY=-3 EndZ=0
    g2: LineSegment [constr] StartX=-22 StartY=5 StartZ=0 EndX=-30 EndY=-3 EndZ=0
    g3: LineSegment [constr] StartX=-22 StartY=-3 StartZ=0 EndX=-30 EndY=5 EndZ=0
    g4: GeomPoint [constr] X=-26 Y=1 Z=0
    g5: Circle CenterX=-26 CenterY=1 CenterZ=0 NormalX=0 NormalY=0 NormalZ=1 AngleXU=0 Radius=1.35
    g6: LineSegment [constr] StartX=-30 StartY=5 StartZ=0 EndX=-30 EndY=-3 EndZ=0
  constraints (15):
    c: Coincident(g0,g-3)
    c: Coincident(g1,g-3)
    c: Horizontal(g0)
    c: Horizontal(g1)
    c: Coincident(g2,g0)
    c: Coincident(g2,g1)
    c: Coincident(g3,g1)
    c: Coincident(g3,g0)
    c: Symmetric(g3,g3,g4)
    c: Diameter(g5) = 2.7
    c: Coincident(g5,g4)
    c: Coincident(g6,g0)
    c: Coincident(g6,g1)
    c: Vertical(g6)
    c: Equal(g0,g6)
FEATURE [PartDesign::Pocket] Pocket009  label="Screw hole001"
  BaseFeature = -> Pad004
  Direction = (-1.487e-13,1,-2.9e-15)
  Length = 5
  Length2 = 5
  Placement = pos=(0,0,0) rot=(1,0,0;1.5708rad)
  Profile = -> Sketch015
  ReferenceAxis = -> Sketch015 [N_Axis]
  Refine = true
  Suppressed = false
  Type = 2
FEATURE [PartDesign::ShapeBinder] ShapeBinder
  Support = -> [Pocket009]
  TraceSupport = false
FEATURE [Sketcher::SketchObject] Sketch016
  ArcFitTolerance = 1e-06
  AttachmentSupport = -> [XZ_Plane006]
  ExternalGeometry = -> [ShapeBinder]
  FullyConstrained = true
  MakeInternals = false
  MapMode = 5
  Placement = pos=(0,0,0) rot=(1,0,0;1.5708rad)
  sketch-geometry (11):
    g0: LineSegment StartX=-21.3716 StartY=17.5 StartZ=0 EndX=-30 EndY=17.5 EndZ=0
    g1: LineSegment StartX=-30 StartY=17.5 StartZ=0 EndX=-30 EndY=-7.5 EndZ=0
    g2: LineSegment StartX=-30 StartY=-7.5 StartZ=0 EndX=-21.3716 EndY=-16.1284 EndZ=0
    g3: LineSegment StartX=-21.3716 StartY=15.3 StartZ=0 EndX=27.8 EndY=15.3 EndZ=0
    g4: LineSegment StartX=27.8 StartY=15.3 StartZ=0 EndX=27.8 EndY=-6.58873 EndZ=0
    g5: LineSegment StartX=-21.3716 StartY=-13.3 StartZ=0 EndX=21.0887 EndY=-13.3 EndZ=0
    g6: LineSegment [constr] StartX=-21.1716 StartY=17.5 StartZ=0 EndX=-21.1716 EndY=-16.3284 EndZ=0
    g7: LineSegment [constr] StartX=-21.3716 StartY=-16.1284 StartZ=0 EndX=-21.3716 EndY=17.5 EndZ=0
    g8: LineSegment StartX=-21.3716 StartY=-16.1284 StartZ=0 EndX=-21.3716 EndY=-13.3 EndZ=0
    g9: LineSegment StartX=-21.3716 StartY=15.3 StartZ=0 EndX=-21.3716 EndY=17.5 EndZ=0
    g10: LineSegment StartX=21.0887 StartY=-13.3 StartZ=0 EndX=27.8 EndY=-6.58873 EndZ=0
  constraints (31):
    c: Coincident(g0,g-6)
    c: Coincident(g1,g0)
    c: Coincident(g1,g-7)
    c: Coincident(g2,g1)
    c: Horizontal(g3)
    c: Distance(g-3,g3) = 0.2
    c: Vertical(g4)
    c: Horizontal(g5)
    c: Distance(g4,g-11) = 0.2
    c: Coincident(g3,g4)
    c: Coincident(g6,g-5)
    c: Coincident(g6,g-8)
    c: Vertical(g7)
    c: Distance(g7,g6) = 0.2
    c: Coincident(g2,g7)
    c: Coincident(g0,g7)
    c: PointOnObject(g5,g7)
    c: PointOnObject(g3,g7)
    c: Distance(g5,g-9) = 0.2
    c: Coincident(g8,g2)
    c: Coincident(g8,g5)
    c: Coincident(g9,g3)
    c: Coincident(g9,g0)
    c: Parallel(g10,g-10)
    c: Distance(g-10,g10) = 0.2
    c: PointOnObject(g10,g5)
    c: PointOnObject(g5,g10)
    c: PointOnObject(g10,g4)
    c: PointOnObject(g4,g10)
    c: Parallel(g2,g-7)
    c: Horizontal(g0)
FEATURE [PartDesign::Pad] Pad005
  Direction = (0,-1,2e-16)
  Length = 4
  Length2 = 10
  Placement = pos=(0,0,0) rot=(1,0,0;1.5708rad)
  Profile = -> Sketch016
  ReferenceAxis = -> Sketch016 [N_Axis]
  Refine = true
  Suppressed = false
  Type = 0
FEATURE [PartDesign::Plane] DatumPlane001  label="Side shapes start"
  AttachmentSupport = -> [Pad005]
  Length = 60
  MapMode = 5
  Placement = pos=(-21.3716,0,2.69e-14) rot=(-0.707107,0,0.707107;3.14159rad)
  ResizeMode = 0
  Width = 60
FEATURE [Sketcher::SketchObject] Sketch017
  ArcFitTolerance = 1e-06
  AttachmentSupport = -> [DatumPlane001]
  ExternalGeometry = -> [Sketch016]
  FullyConstrained = true
  MakeInternals = false
  MapMode = 5
  Placement = pos=(-21.3716,0,2.69e-14) rot=(-0.707107,0,0.707107;3.14159rad)
  sketch-geometry (4):
    g0: LineSegment StartX=13.3 StartY=3e-15 StartZ=0 EndX=11.3 EndY=2 EndZ=0
    g1: LineSegment StartX=11.3 StartY=2 StartZ=0 EndX=11.3 EndY=4 EndZ=0
    g2: LineSegment StartX=11.3 StartY=4 StartZ=0 EndX=13.3 EndY=4 EndZ=0
    g3: LineSegment StartX=13.3 StartY=4 StartZ=0 EndX=13.3 EndY=3.1e-15 EndZ=0
  constraints (11):
    c: Vertical(g1)
    c: Coincident(g2,g1)
    c: Coincident(g3,g2)
    c: Coincident(g0,g3)
    c: Angle(g3,g0) = 0.785398
    c: Distance(g0,g1) = 2
    c: Coincident(g1,g0)
    c: Horizontal(g2)
    c: Coincident(g0,g-3)
    c: Vertical(g3)
    c: Equal(g1,g2)
FEATURE [PartDesign::Pocket] Pocket010  label="Left side"
  BaseFeature = -> Pad005
  Direction = (1,0,-1.4e-15)
  Length = 5
  Length2 = 5
  Placement = pos=(0,0,0) rot=(1,0,0;1.5708rad)
  Profile = -> Sketch017
  ReferenceAxis = -> Sketch017 [N_Axis]
  Refine = true
  Suppressed = false
  Type = 1
FEATURE [Sketcher::SketchObject] Sketch018
  ArcFitTolerance = 1e-06
  AttachmentSupport = -> [DatumPlane001]
  ExternalGeometry = -> [Sketch016]
  FullyConstrained = true
  MakeInternals = false
  MapMode = 5
  Placement = pos=(-21.3716,0,2.69e-14) rot=(-0.707107,0,0.707107;3.14159rad)
  sketch-geometry (4):
    g0: LineSegment StartX=-15.3 StartY=4 StartZ=0 EndX=-15.3 EndY=-3.1e-15 EndZ=0
    g1: LineSegment StartX=-15.3 StartY=4 StartZ=0 EndX=-13.3 EndY=4 EndZ=0
    g2: LineSegment StartX=-13.3 StartY=4 StartZ=0 EndX=-13.3 EndY=2 EndZ=0
    g3: LineSegment StartX=-13.3 StartY=2 StartZ=0 EndX=-15.3 EndY=-3.1e-15 EndZ=0
  constraints (11):
    c: Coincident(g1,g0)
    c: Coincident(g2,g1)
    c: Vertical(g2)
    c: Coincident(g3,g2)
    c: Coincident(g3,g0)
    c: Distance(g2,g1) = 2
    c: Angle(g3,g0) = 0.785398
    c: Coincident(g0,g-3)
    c: Vertical(g0)
    c: Horizontal(g1)
    c: Equal(g2,g1)
FEATURE [PartDesign::Pocket] Pocket011  label="Right side"
  BaseFeature = -> Pocket010
  Direction = (1,0,-1.4e-15)
  Length = 5
  Length2 = 5
  Placement = pos=(0,0,0) rot=(1,0,0;1.5708rad)
  Profile = -> Sketch018
  ReferenceAxis = -> Sketch018 [N_Axis]
  Refine = true
  Suppressed = false
  Type = 1
FEATURE [PartDesign::Line] DatumLine001  label="Hole axis"
  AttacherType = Attacher::AttachEngineLine
  AttachmentSupport = -> [ShapeBinder]
  Length = 20
  MapMode = 19
  Placement = pos=(-26,-41,1) rot=(1,0,0;1.5708rad)
  ResizeMode = 0
FEATURE [PartDesign::Plane] DatumPlane002  label="Hole sketch plane"
  AttachmentSupport = -> [DatumLine001]
  Length = 70.1528
  MapMode = 3
  Placement = pos=(-26,-41,1) rot=(1,0,0;3.14159rad)
  ResizeMode = 0
  Width = 78.3528
FEATURE [Sketcher::SketchObject] Sketch020
  ArcFitTolerance = 1e-06
  AttachmentSupport = -> [DatumPlane002]
  ExternalGeometry = -> [Pocket011,DatumLine001]
  FullyConstrained = true
  MakeInternals = false
  MapMode = 5
  Placement = pos=(-26,-41,1) rot=(1,0,0;3.14159rad)
  expr: Constraints[6] = Spreadsheet.ScrewHeadRadius
  expr: Constraints[7] = Spreadsheet.ScrewHoleRadius
  sketch-geometry (6):
    g0: LineSegment StartX=0 StartY=-41 StartZ=0 EndX=0 EndY=-37 EndZ=0
    g1: LineSegment StartX=3 StartY=-40 StartZ=0 EndX=3 EndY=-37 EndZ=0
    g2: LineSegment StartX=3 StartY=-40 StartZ=0 EndX=1.7 EndY=-40 EndZ=0
    g3: LineSegment StartX=1.7 StartY=-41 StartZ=0 EndX=1.7 EndY=-40 EndZ=0
    g4: LineSegment StartX=1.7 StartY=-41 StartZ=0 EndX=0 EndY=-41 EndZ=0
    g5: LineSegment StartX=0 StartY=-37 StartZ=0 EndX=3 EndY=-37 EndZ=0
  constraints (18):
    c: Vertical(g0)
    c: Vertical(g1)
    c: Vertical(g3)
    c: Coincident(g4,g0)
    c: Coincident(g5,g0)
    c: Horizontal(g5)
    c: DistanceX(g0,g1) = 3
    c: DistanceX(g0,g3) = 1.7
    c: DistanceY(g1,g1) = 3
    c: Coincident(g2,g1)
    c: Coincident(g2,g3)
    c: Coincident(g4,g3)
    c: Coincident(g5,g1)
    c: PointOnObject(g0,g-3)
    c: PointOnObject(g0,g-5)
    c: PointOnObject(g3,g-3)
    c: PointOnObject(g0,g-4)
    c: DistanceY(g3,g2) = 1
FEATURE [PartDesign::Groove] Groove  label="Screw hole"
  Angle = 360
  Angle2 = 60
  Axis = (1.49e-13,-1,2.9e-15)
  Base = (-26,-41,1)
  BaseFeature = -> Pocket011
  Placement = pos=(0,0,0) rot=(1,0,0;1.5708rad)
  Profile = -> Sketch020
  ReferenceAxis = -> Sketch020 [V_Axis]
  Refine = true
  Suppressed = false
  Type = 0
FEATURE [PartDesign::Body] Body005  label="Lid"
  AllowCompound = false
  Group = -> [ShapeBinder,Sketch016,Pad005,DatumPlane001,Sketch017,Pocket010,Sketch018,Pocket011,DatumLine001,DatumPlane002,Sketch020,Groove]
  Origin = -> Origin006
  Tip = -> Groove
FEATURE [Part::Part2DObjectPython] ShapeString  label="StringShort"  # Draft 2D object (typed FeaturePython)
  FontFile = <userpath>/Documents/3D/multimeter_module/Orbitron-VariableFont_wght.ttf
  Fuse = false
  Justification = 3
  JustificationReference = 0
  KeepLeftMargin = false
  MakeFace = true
  ObliqueAngle = 0
  Placement = pos=(-5,-39,17.5) rot=(0,0,1;1.5708rad)
  ScaleToSize = true
  Size = 6
  String = short
  Tracking = 0
FEATURE [Part::Part2DObjectPython] ShapeString001  label="StringConnect"  # Draft 2D object (typed FeaturePython)
  FontFile = <userpath>/Documents/3D/multimeter_module/Orbitron-VariableFont_wght.ttf
  Fuse = false
  Justification = 3
  JustificationReference = 0
  KeepLeftMargin = false
  MakeFace = true
  ObliqueAngle = 0
  Placement = pos=(14,-39,17.5) rot=(0,0,1;1.5708rad)
  ScaleToSize = true
  Size = 6
  String = connect
  Tracking = 0
FEATURE [Sketcher::SketchObject] Sketch022
  ArcFitTolerance = 1e-06
  AttachmentSupport = -> [Pocket009]
  ExternalGeometry = -> [Pocket009]
  FullyConstrained = true
  MakeInternals = false
  MapMode = 5
  Placement = pos=(0,7.7e-15,17.5) rot=(0,0,1;3.14159rad)
  expr: Constraints[17] = Spreadsheet.PlugDistance
  expr: Constraints[4] = Spreadsheet.PlugOffset
  sketch-geometry (10):
    g0: LineSegment StartX=-18.5 StartY=7.7e-15 StartZ=0 EndX=-18.5 EndY=37 EndZ=0
    g1: LineSegment StartX=-9.5 StartY=7.7e-15 StartZ=0 EndX=-9.5 EndY=37 EndZ=0
    g2: LineSegment [constr] StartX=-14 StartY=7.7e-15 StartZ=0 EndX=-14 EndY=37 EndZ=0
    g3: ArcOfCircle CenterX=-14 CenterY=37 CenterZ=0 NormalX=0 NormalY=0 NormalZ=1 AngleXU=0 Radius=4.5 StartAngle=6e-16 EndAngle=3.14159
    g4: LineSegment [constr] StartX=5 StartY=7.7e-15 StartZ=0 EndX=5 EndY=37 EndZ=0
    g5: LineSegment StartX=0.5 StartY=7.7e-15 StartZ=0 EndX=0.5 EndY=37 EndZ=0
    g6: LineSegment StartX=9.5 StartY=7.7e-15 StartZ=0 EndX=9.5 EndY=37 EndZ=0
    g7: ArcOfCircle CenterX=5 CenterY=37 CenterZ=0 NormalX=0 NormalY=0 NormalZ=1 AngleXU=0 Radius=4.5 StartAngle=-9e-16 EndAngle=3.14159
    g8: LineSegment StartX=-18.5 StartY=7.7e-15 StartZ=0 EndX=-9.5 EndY=7.7e-15 EndZ=0
    g9: LineSegment StartX=0.5 StartY=7.7e-15 StartZ=0 EndX=9.5 EndY=7.7e-15 EndZ=0
  constraints (30):
    c: Vertical(g0)
    c: Vertical(g1)
    c: Vertical(g2)
    c: PointOnObject(g2,g-3)
    c: DistanceX(g-4,g2) = 16
    c: Distance(g2,g2) = 37
    c: PointOnObject(g0,g-3)
    c: Distance(g1,g0) = 9
    c: Symmetric(g1,g0,g2)
    c: Equal(g1,g2)
    c: Coincident(g1,g3)
    c: Coincident(g0,g3)
    c: Coincident(g3,g2)
    c: PointOnObject(g4,g-3)
    c: Vertical(g4)
    c: PointOnObject(g5,g-3)
    c: Vertical(g5)
    c: Distance(g2,g4) = 19
    c: Symmetric(g5,g6,g4)
    c: Equal(g4,g2)
    c: Equal(g5,g2)
    c: Equal(g6,g2)
    c: Coincident(g7,g4)
    c: Coincident(g7,g6)
    c: Coincident(g7,g5)
    c: Distance(g6,g5) = 9
    c: Coincident(g8,g0)
    c: Coincident(g8,g1)
    c: Coincident(g9,g5)
    c: Coincident(g9,g6)
FEATURE [PartDesign::Pocket] Pocket012  label="TextPockets"
  BaseFeature = -> Pocket009
  Direction = (0,0,-1)
  Length = 0.5
  Length2 = 5
  Placement = pos=(0,0,0) rot=(1,0,0;1.5708rad)
  Profile = -> Sketch022
  ReferenceAxis = -> Sketch022 [N_Axis]
  Refine = true
  Suppressed = false
  Type = 0
FEATURE [PartDesign::Body] Body  label="Box0"
  AllowCompound = false
  Group = -> [Sketch,Pad,Sketch001,Pocket,Sketch003,Pocket001,Sketch004,Pocket002,Sketch005,Pocket003,Sketch006,Pocket004,Sketch007,Pocket005,Pad007,Sketch021,DatumPlane,Mirrored,Sketch008,Pocket006,Sketch009,Pad001,Mirrored001,Mirrored002,Sketch013,Pocket008,Sketch014,Pad004,Sketch015,Pocket009,Sketch022,Pocket012,ShapeString001,ShapeString]
  Origin = -> Origin
  Tip = -> Pocket012
FEATURE [Part::Extrusion] Extrude002  label="TextConnect"
  Base = -> ShapeString001
  Dir = (0,0,1)
  DirMode = 2
  FaceMakerClass = Part::FaceMakerBullseye
  FaceMakerMode = 3
  LengthFwd = 1
  LengthRev = 0
  Placement = pos=(0,0,-1) rot=(0,0,1;0rad)
  Solid = false
  Symmetric = false
FEATURE [Part::Extrusion] Extrude003  label="TextShort"
  Base = -> ShapeString
  Dir = (0,0,1)
  DirMode = 2
  FaceMakerClass = Part::FaceMakerBullseye
  FaceMakerMode = 3
  LengthFwd = 1
  LengthRev = 0
  Placement = pos=(0,0,-1) rot=(0,0,1;0rad)
  Solid = false
  Symmetric = false
FEATURE [Part::MultiFuse] Fusion  label="Box"
  Shapes = -> [Body,Extrude002,Extrude003]
FEATURE [App::FeaturePython] Joint013  label="Revolute002"  # Assembly joint (typed FeaturePython)
  Activated = true
  AngleMax = 0
  AngleMin = 0
  Detach1 = false
  Detach2 = false
  Distance = 0
  Distance2 = 0
  EnableAngleMax = true
  EnableAngleMin = true
  EnableLengthMax = false
  EnableLengthMin = false
  JointType = 1 (Revolute)
  LengthMax = 0
  LengthMin = 0
  Placement1 = pos=(-26,-41,1) rot=(1,0,0;1.5708rad)
  Placement2 = pos=(-26,-3.055e-13,1) rot=(1,0,0;1.5708rad)
  Reference1 = -> Assembly [Box.Edge121,Box.Edge121]
  Reference2 = -> Assembly [Lid.Edge18,Lid.Edge18]
FEATURE [Assembly::JointGroup] Joints
  Group = -> [GroundedJoint,Joint001,Joint002,Joint013,Joint014,Joint015,Joint,Joint016,Joint017]
FEATURE [Assembly::AssemblyObject] Assembly
  Group = -> [Joints,Box,GroundedJoint,Fuse_holder_BK8_HTC_603M001,Switch_a8l_11_15n11,Switch_a8l_11_15n012,Socket_4mm,Socket_4mm001,Joint001,Joint002,Plug_4mm,Plug_4mm001,Lid,Joint013,Joint014,Joint015,Joint,Joint016,Joint017]
  Origin = -> Origin001
  Type = Assembly
FEATURE [Part::FeaturePython] Point  label="Socket- point"  # WARN: FeaturePython — macro-defined, semantics opaque (R4)
  Placement = pos=(-20,-17,12) rot=(0,0,1;0rad)
  X = -20
  Y = -17
  Z = 12
FEATURE [Part::FeaturePython] Point001  label="Socket+ point"  # WARN: FeaturePython — macro-defined, semantics opaque (R4)
  Placement = pos=(-20,-33,12) rot=(0,0,1;0rad)
  X = -20
  Y = -33
  Z = 12
FEATURE [Part::FeaturePython] Point002  label="Plug COM point"  # WARN: FeaturePython — macro-defined, semantics opaque (R4)
  Placement = pos=(-5,-22,-13) rot=(0,0,1;0rad)
  X = -5
  Y = -22
  Z = -13
FEATURE [Part::FeaturePython] Point003  label="Plug mA point"  # WARN: FeaturePython — macro-defined, semantics opaque (R4)
  Placement = pos=(14,-22,-13) rot=(0,0,1;0rad)
  X = 14
  Y = -22
  Z = -13
FEATURE [Part::FeaturePython] Point004  label="Switch SHORT lower point"  # WARN: FeaturePython — macro-defined, semantics opaque (R4)
  Placement = pos=(-0.5,-21,-4) rot=(0,0,1;0rad)
  X = -0.5
  Y = -21
  Z = -4
FEATURE [Part::FeaturePython] Point005  label="Switch SHORT upper point"  # WARN: FeaturePython — macro-defined, semantics opaque (R4)
  Placement = pos=(-0.5,-21,6) rot=(0,0,1;0rad)
  X = -0.5
  Y = -21
  Z = 6
FEATURE [Part::FeaturePython] Point006  label="Switch CONNECT lower point"  # WARN: FeaturePython — macro-defined, semantics opaque (R4)
  Placement = pos=(9.5,-21,-4) rot=(0,0,1;0rad)
  X = 9.5
  Y = -21
  Z = -4
FEATURE [Part::FeaturePython] Point007  label="Switch CONNECT upper point"  # WARN: FeaturePython — macro-defined, semantics opaque (R4)
  Placement = pos=(9.5,-21,6) rot=(0,0,1;0rad)
  X = 9.5
  Y = -21
  Z = 6
FEATURE [Part::FeaturePython] Point008  label="Fuse left point"  # WARN: FeaturePython — macro-defined, semantics opaque (R4)
  Placement = pos=(4,-29,5) rot=(0,0,1;0rad)
  X = 4
  Y = -29
  Z = 5
FEATURE [Part::FeaturePython] Point009  label="Fuse right point"  # WARN: FeaturePython — macro-defined, semantics opaque (R4)
  Placement = pos=(14,-36,5) rot=(0,0,1;0rad)
  X = 14
  Y = -36
  Z = 5
FEATURE [Part::Part2DObjectPython] Line002  label="WireFlex002"  # Draft 2D object (typed FeaturePython)
  Area = 0
  ChamferSize = 0
  Closed = false
  End = (9.5,-21,6)
  FilletRadius = 0
  Length = 10
  MakeFace = false
  Placement = pos=(-0.5,-21,6) rot=(0,0,1;0rad)
  Points = (2) [(0,0,0),(10,0,0)]
  Start = (-0.5,-21,6)
  Subdivisions = 0
  Vrtx_end = -> Point007
  Vrtx_start = -> Point005
FEATURE [Part::Part2DObjectPython] Line003  label="WireFlex003"  # Draft 2D object (typed FeaturePython)
  Area = 0
  ChamferSize = 0
  Closed = false
  End = (-20,-33,12)
  FilletRadius = 0
  Length = 35.6406
  MakeFace = false
  Placement = pos=(9.5,-21,-4) rot=(0,0,1;0rad)
  Points = (2) [(0,0,0),(-29.5,-12,16)]
  Start = (9.5,-21,-4)
  Subdivisions = 0
  Vrtx_end = -> Point001
  Vrtx_start = -> Point006
FEATURE [Part::Part2DObjectPython] Line004  label="WireFlex004"  # Draft 2D object (typed FeaturePython)
  Area = 0
  ChamferSize = 0
  Closed = false
  End = (4,-29,5)
  FilletRadius = 0
  Length = 9.75961
  MakeFace = false
  Placement = pos=(9.5,-21,6) rot=(0,0,1;0rad)
  Points = (2) [(0,0,0),(-5.5,-8,-1)]
  Start = (9.5,-21,6)
  Subdivisions = 0
  Vrtx_end = -> Point008
  Vrtx_start = -> Point007
FEATURE [Part::Part2DObjectPython] Line005  label="WireFlex005"  # Draft 2D object (typed FeaturePython)
  Area = 0
  ChamferSize = 0
  Closed = false
  End = (14,-36,5)
  FilletRadius = 0
  Length = 22.8035
  MakeFace = false
  Placement = pos=(14,-22,-13) rot=(0,0,1;0rad)
  Points = (2) [(0,0,0),(0,-14,18)]
  Start = (14,-22,-13)
  Subdivisions = 0
  Vrtx_end = -> Point009
  Vrtx_start = -> Point003
FEATURE [Part::FeaturePython] Point010  label="Point"  # WARN: FeaturePython — macro-defined, semantics opaque (R4)
  Placement = pos=(-5,-25,-13) rot=(0,0,1;0rad)
  X = -5
  Y = -25
  Z = -13
FEATURE [Part::Part2DObjectPython] Wire  label="WireFlex006"  # Draft 2D object (typed FeaturePython)
  Area = 0
  ChamferSize = 0
  Closed = false
  End = (-20,-17,12)
  FilletRadius = 0
  Length = 33.2324
  MakeFace = false
  Placement = pos=(-5,-22,-13) rot=(0,0,1;0rad)
  Points = (3) [(0,0,0),(0,-3,0),(-15,5,25)]
  Start = (-5,-22,-13)
  Subdivisions = 0
  Vrtx_end = -> Point
  Vrtx_start = -> Point002
  Vrtxs_mid = -> [Point010]
  Vrtxs_mid_idx = [2]
FEATURE [Part::Part2DObjectPython] Wire001  label="WireFlex"  # Draft 2D object (typed FeaturePython)
  Area = 0
  ChamferSize = 0
  Closed = false
  End = (-0.5,-21,-4)
  FilletRadius = 0
  Length = 13.8282
  MakeFace = false
  Placement = pos=(-5,-22,-13) rot=(0,0,1;0rad)
  Points = (3) [(0,0,0),(0,-3,0),(4.5,1,9)]
  Start = (-5,-22,-13)
  Subdivisions = 0
  Vrtx_end = -> Point004
  Vrtx_start = -> Point002
  Vrtxs_mid = -> [Point010]
  Vrtxs_mid_idx = [2]
FEATURE [App::DocumentObjectGroup] Group001  label="Wiring"
  Group = -> [Point,Point001,Point003,Point002,Point004,Point005,Point006,Point007,Point008,Point009,Point010,Line005,Line004,Line003,Line002,Wire,Wire001]
